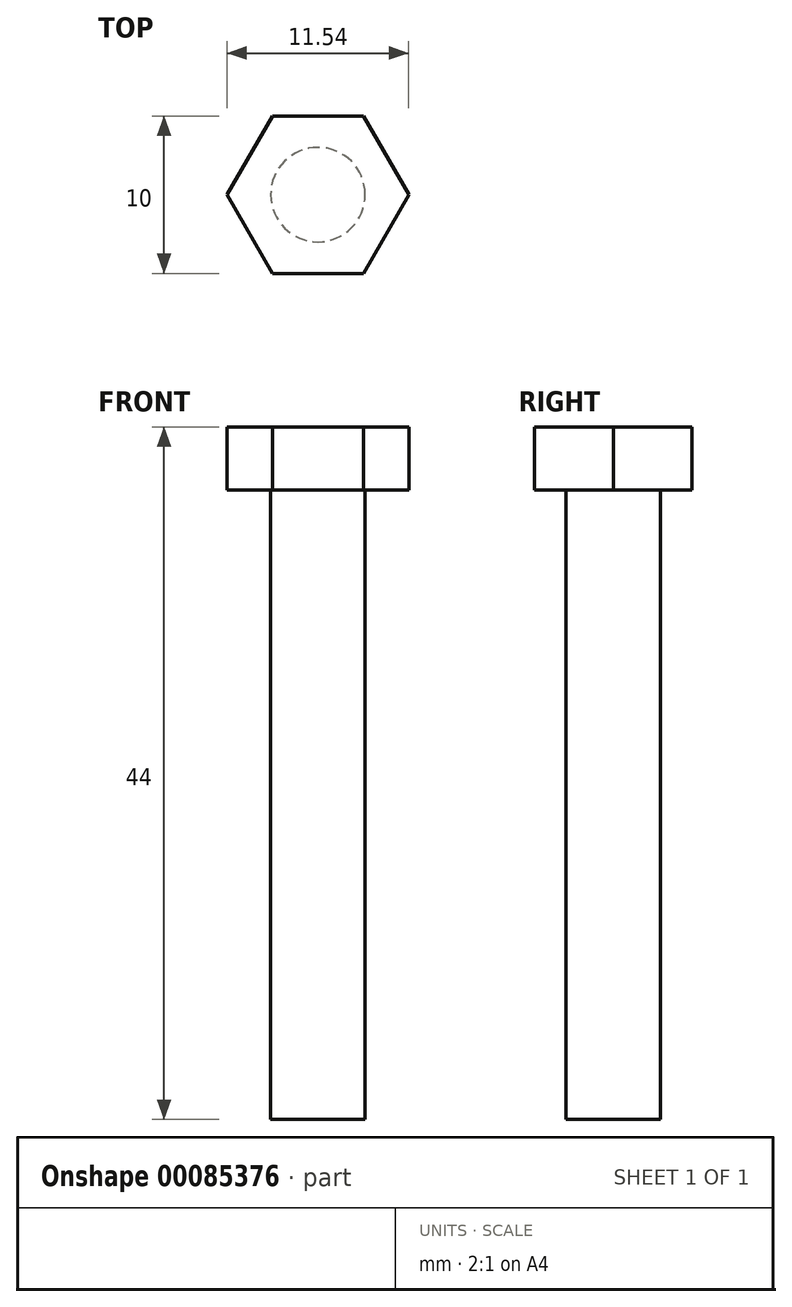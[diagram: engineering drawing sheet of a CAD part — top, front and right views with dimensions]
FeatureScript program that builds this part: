
annotation { "Feature Type Name" : "Feature", "Feature Type Description" : "" }
export const myFeature = defineFeature(function(context is Context, id is Id, definition is map)
    precondition{}
    {
        {
            var Q0;
            Q0=qCreatedBy(makeId("Top.planeOp"),FACE);
            var sketch = newSketch(context, id + "F0", { "sketchPlane" : qUnion([Q0])});
            skCircle(sketch, "E0", {"center": v(0, 0) * mm, "radius": 3 * mm});
            skCircle(sketch, "E1.cCircle", {"center": v(0, 0) * mm, "radius": 5 * mm, "construction": true});
            skLineSegment(sketch, "E1.0", {"start": v(-2.89, 5) * mm, "end": v(2.89, 5) * mm});
            skLineSegment(sketch, "E1.1", {"start": v(2.89, 5) * mm, "end": v(5.77, 0) * mm});
            skLineSegment(sketch, "E1.2", {"start": v(5.77, 0) * mm, "end": v(2.89, -5) * mm});
            skLineSegment(sketch, "E1.3", {"start": v(2.89, -5) * mm, "end": v(-2.89, -5) * mm});
            skLineSegment(sketch, "E1.4", {"start": v(-2.89, -5) * mm, "end": v(-5.77, 0) * mm});
            skLineSegment(sketch, "E1.5", {"start": v(-5.77, 0) * mm, "end": v(-2.89, 5) * mm});
            skPoint(sketch, "E1.0.midPoint", {"position": v(0, 5) * mm});
            skSolve(sketch);
        }
        {
            var Q0;
            Q0=makeQuery(id+"F0.imprint","IMPRINT",FACE,{"disambiguationData":[TD([[makeQuery(id+"F0.imprint","IMPRINT",EDGE,{"derivedFrom":sQuery(id+"F0.wireOp",EDGE,"E0")}),1.0]])]});
            var Q1;
            Q1=makeQuery(id+"F0.imprint","IMPRINT",FACE,{"disambiguationData":[TD([[makeQuery(id+"F0.imprint","IMPRINT",EDGE,{"derivedFrom":sQuery(id+"F0.wireOp",EDGE,"E0")}),-1.0]])]});
            extrude(context, id + "F1", {"entities" : qUnion([Q0, Q1]), "depth" : 4 * mm});
        }
        {
            var Q0;
            Q0=makeQuery(id+"F0.imprint","IMPRINT",FACE,{"disambiguationData":[TD([[makeQuery(id+"F0.imprint","IMPRINT",EDGE,{"derivedFrom":sQuery(id+"F0.wireOp",EDGE,"E0")}),1.0]])]});
            extrude(context, id + "F2", {"entities" : qUnion([Q0]), "operationType" : NewBodyOperationType.ADD, "oppositeDirection" : true, "depth" : 40 * mm});
        }
    });
